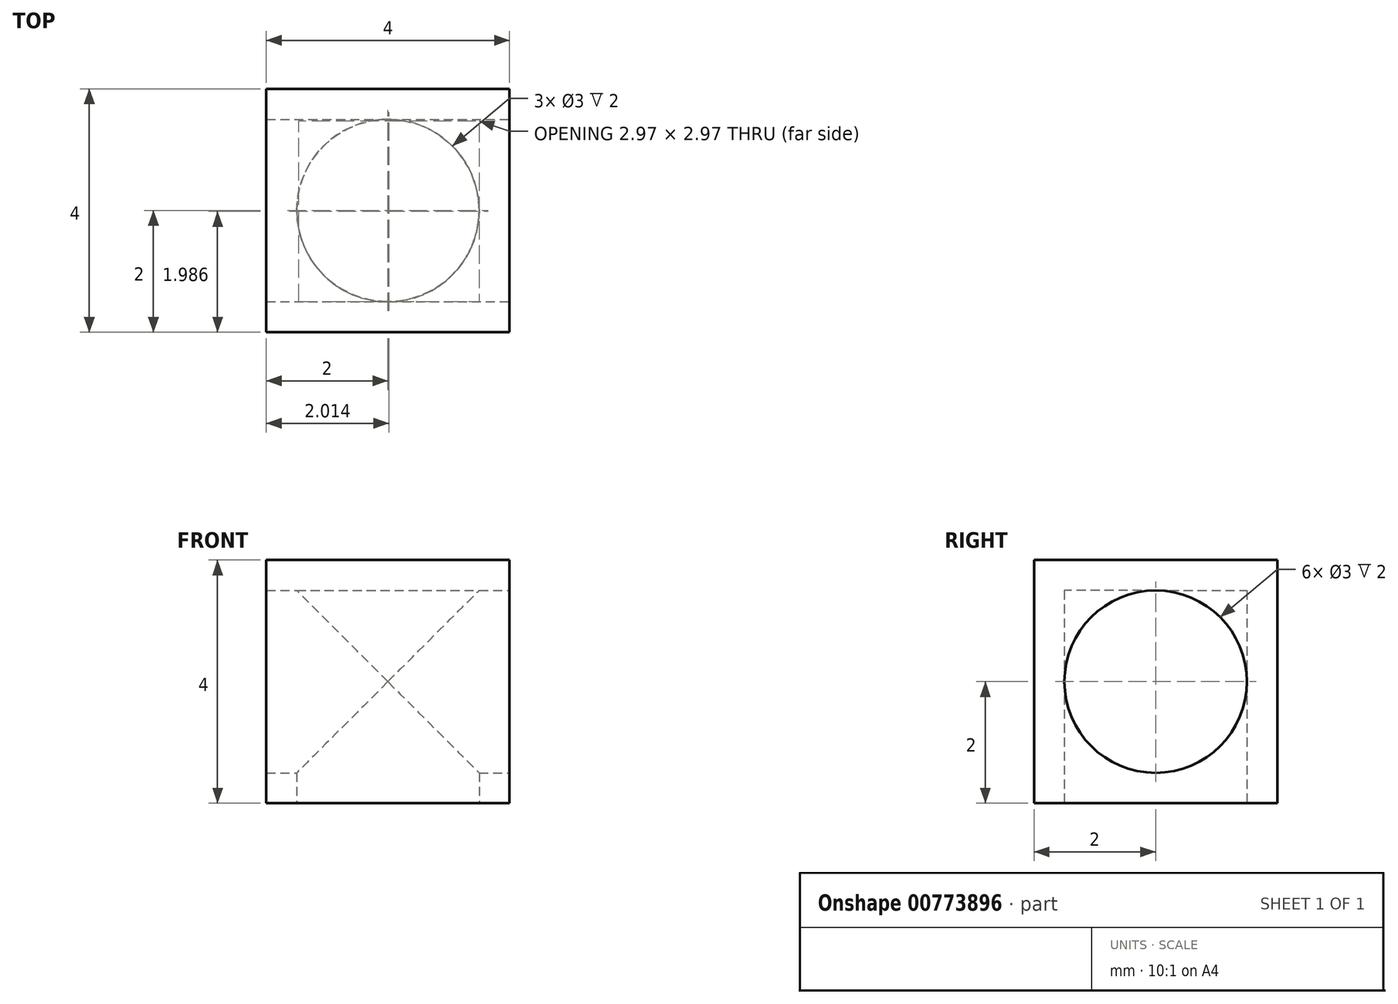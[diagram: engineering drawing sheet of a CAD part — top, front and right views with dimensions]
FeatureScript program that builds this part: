
annotation { "Feature Type Name" : "Feature", "Feature Type Description" : "" }
export const myFeature = defineFeature(function(context is Context, id is Id, definition is map)
    precondition{}
    {
        {
            var Q0;
            Q0=qCreatedBy(makeId("Top.planeOp"),FACE);
            var sketch = newSketch(context, id + "F0", { "sketchPlane" : qUnion([Q0])});
            skLineSegment(sketch, "E0.bottom", {"start": v(2, 2) * mm, "end": v(-2, 2) * mm});
            skLineSegment(sketch, "E0.top", {"start": v(2, -2) * mm, "end": v(-2, -2) * mm});
            skLineSegment(sketch, "E0.left", {"start": v(2, 2) * mm, "end": v(2, -2) * mm});
            skLineSegment(sketch, "E0.right", {"start": v(-2, 2) * mm, "end": v(-2, -2) * mm});
            skPoint(sketch, "E0.middle", {"position": v(0, 0) * mm});
            skSolve(sketch);
        }
        {
            var Q0;
            Q0 = qSketchRegion(id + "F0", true);
            extrude(context, id + "F1", {"entities" : qUnion([Q0]), "depth" : 4 * mm, "offsetDistance" : 25.4 * mm});
        }
        {
            var Q0;
            Q0=qCreatedBy(makeId("Top.planeOp"),FACE);
            var sketch = newSketch(context, id + "F2", { "sketchPlane" : qUnion([Q0])});
            skCircle(sketch, "E1", {"center": v(0, 0) * mm, "radius": 1.5 * mm});
            skSolve(sketch);
        }
        {
            var Q0;
            Q0 = qSketchRegion(id + "F2", true);
            extrude(context, id + "F3", {"entities" : qUnion([Q0]), "operationType" : NewBodyOperationType.REMOVE, "depth" : 3.5 * mm, "offsetDistance" : 25.4 * mm});
        }
        {
            var Q0;
            Q0=qCreatedBy(makeId("Right.planeOp"),FACE);
            var sketch = newSketch(context, id + "F4", { "sketchPlane" : qUnion([Q0])});
            skCircle(sketch, "E2", {"center": v(0, 2) * mm, "radius": 1.5 * mm});
            skSolve(sketch);
        }
        {
            var Q0;
            Q0 = qSketchRegion(id + "F4", true);
            extrude(context, id + "F5", {"entities" : qUnion([Q0]), "operationType" : NewBodyOperationType.REMOVE, "oppositeDirection" : true, "depth" : 25.4 * mm, "offsetDistance" : 25.4 * mm, "hasSecondDirection" : true, "secondDirectionOppositeDirection" : false, "secondDirectionDepth" : 25.4 * mm});
        }
    });
